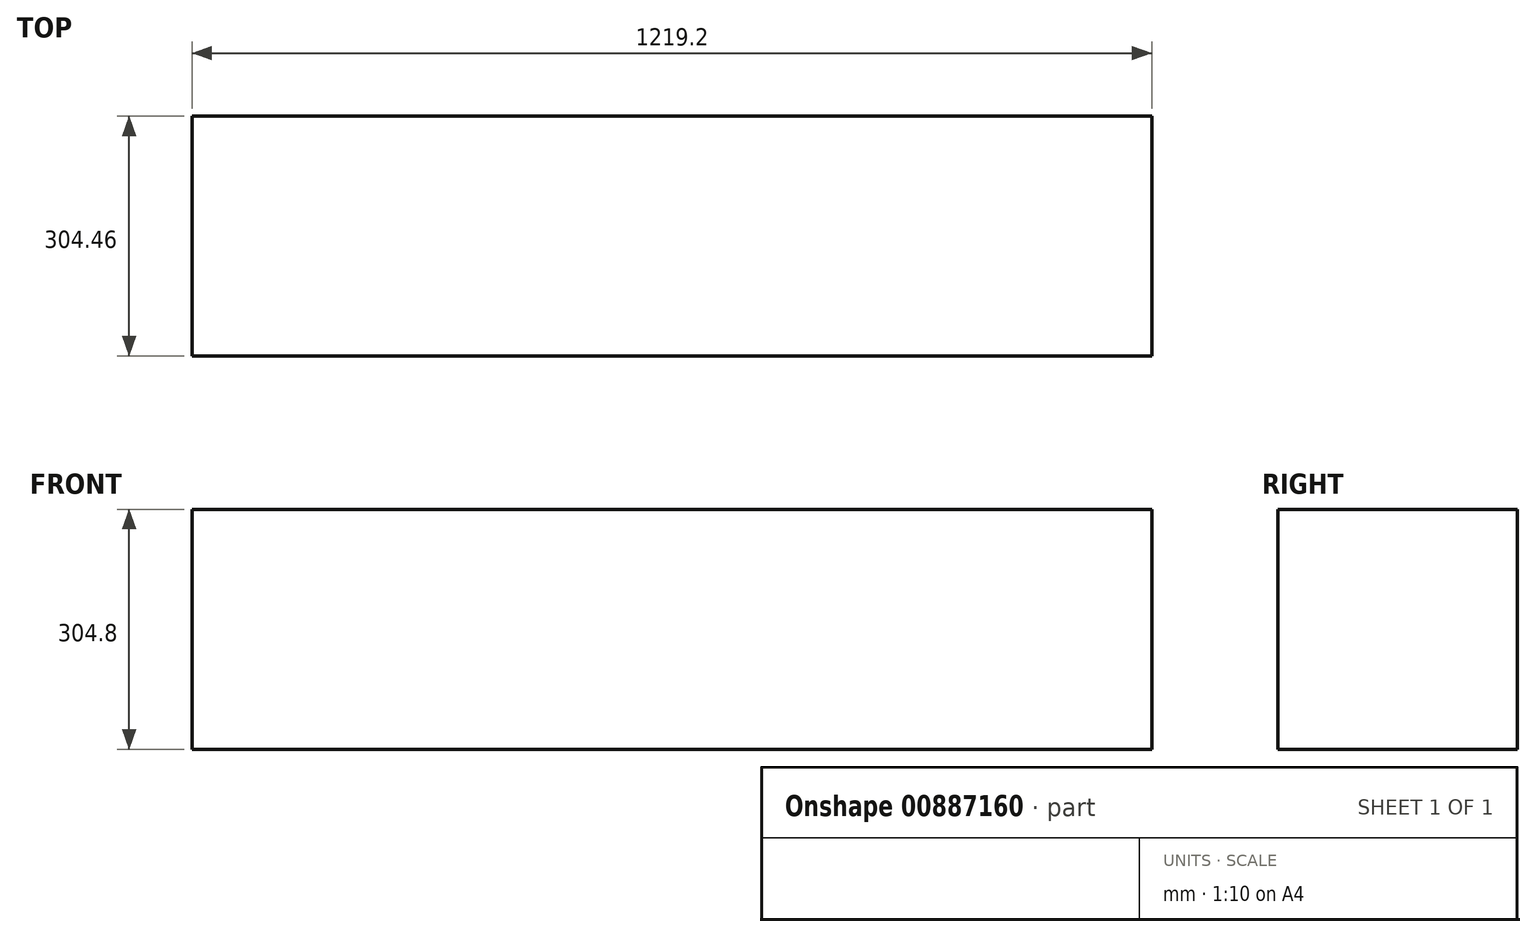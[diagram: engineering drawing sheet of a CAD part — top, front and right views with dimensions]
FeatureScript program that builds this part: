
annotation { "Feature Type Name" : "Feature", "Feature Type Description" : "" }
export const myFeature = defineFeature(function(context is Context, id is Id, definition is map)
    precondition{}
    {
        {
            var Q0;
            Q0=qCreatedBy(makeId("Right.planeOp"),FACE);
            var sketch = newSketch(context, id + "F0", { "sketchPlane" : qUnion([Q0])});
            skLineSegment(sketch, "E0", {"start": v(0, 0) * mm, "end": v(-75.86, 0) * mm});
            skSolve(sketch);
        }
        {
            var Q0;
            Q0=sQuery(id+"F0.wireOp",EDGE,"E0");
            extrude(context, id + "F1", {"bodyType" : ToolBodyType.SURFACE, "surfaceEntities" : qUnion([Q0]), "depth" : 1219.2 * mm, "offsetDistance" : 25.4 * mm});
        }
        {
            var Q0;
            Q0=makeQuery(id+"F1.opExtrude","SWEPT_FACE",FACE,{"disambiguationData":[OSD([sQuery(id+"F0.wireOp",EDGE,"E0")])]});
            extrude(context, id + "F2", {"entities" : qUnion([Q0]), "depth" : 304.8 * mm, "offsetDistance" : 25.4 * mm});
        }
        {
            var Q0;
            Q0=makeQuery(id+"F2.opExtrude","SWEPT_FACE",FACE,{"disambiguationData":[OSD([sQuery(id+"F0.wireOp",VERTEX,"E0.end")])]});
            extrude(context, id + "F3", {"entities" : qUnion([Q0]), "operationType" : NewBodyOperationType.ADD, "depth" : 228.6 * mm, "offsetDistance" : 25.4 * mm});
        }
    });
